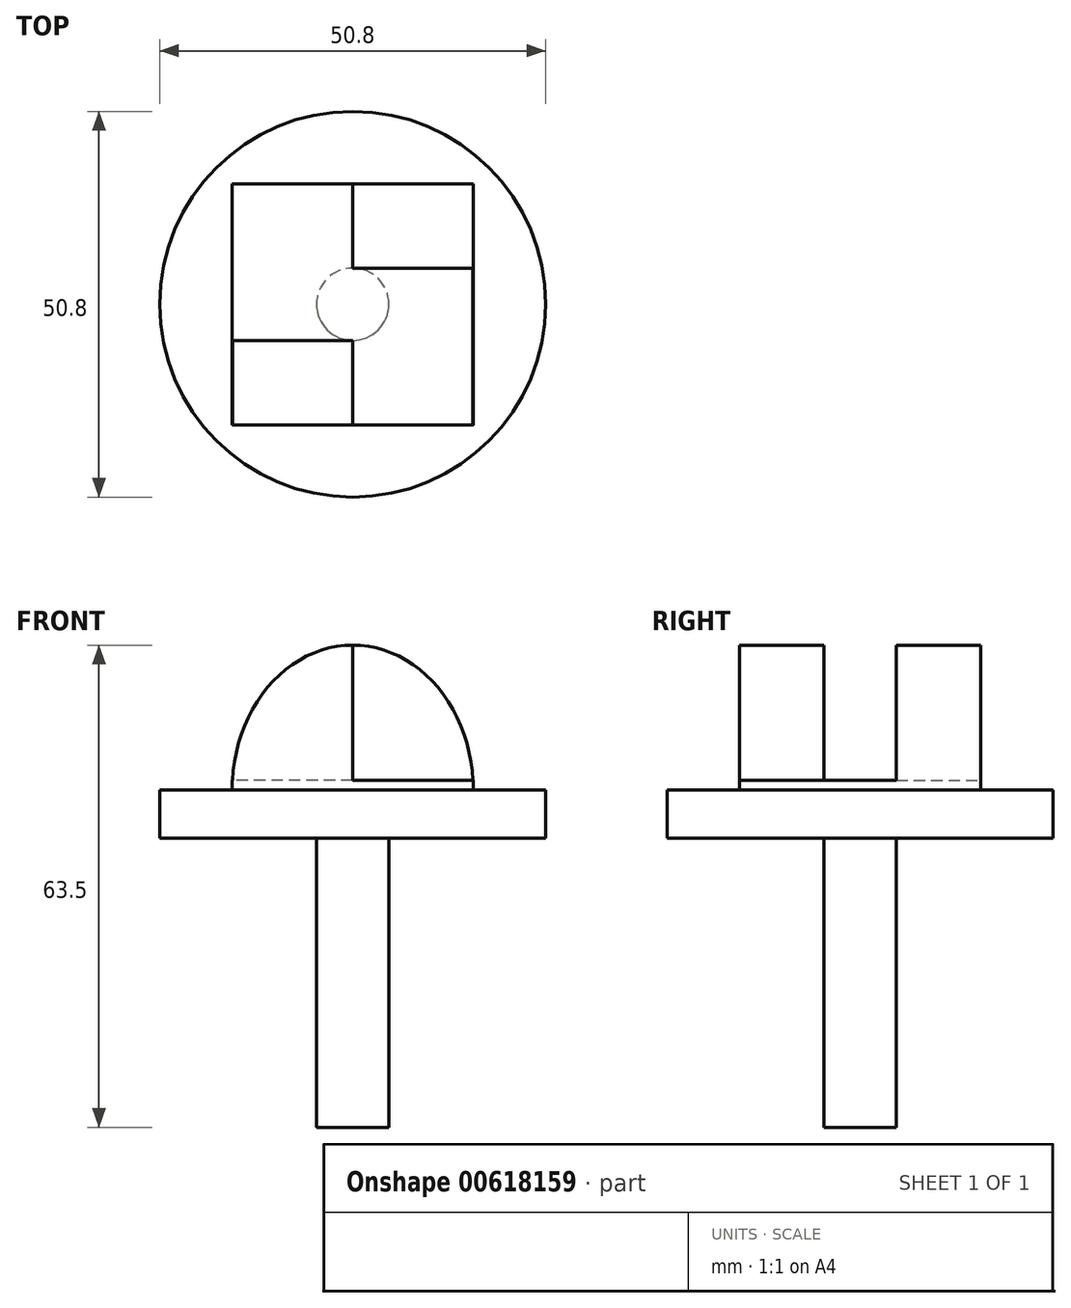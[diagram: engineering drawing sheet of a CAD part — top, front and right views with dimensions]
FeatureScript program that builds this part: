
annotation { "Feature Type Name" : "Feature", "Feature Type Description" : "" }
export const myFeature = defineFeature(function(context is Context, id is Id, definition is map)
    precondition{}
    {
        {
            var Q0;
            Q0=qCreatedBy(makeId("Front.planeOp"),FACE);
            var sketch = newSketch(context, id + "F0", { "sketchPlane" : qUnion([Q0])});
            skLineSegment(sketch, "E0", {"start": v(0, 0) * mm, "end": v(0, 0) * mm});
            skLineSegment(sketch, "E1", {"start": v(0, 0) * mm, "end": v(-4.76, 0) * mm});
            skLineSegment(sketch, "E2", {"start": v(-4.76, -6.35) * mm, "end": v(-4.76, 0) * mm});
            skLineSegment(sketch, "E3", {"start": v(-4.76, -6.35) * mm, "end": v(-25.4, -6.35) * mm});
            skLineSegment(sketch, "E4", {"start": v(-25.4, -6.35) * mm, "end": v(-25.4, 0) * mm});
            skLineSegment(sketch, "E5", {"start": v(-25.4, 0) * mm, "end": v(0, 0) * mm});
            skLineSegment(sketch, "E6", {"start": v(0, 0) * mm, "end": v(0, -6.35) * mm});
            skSolve(sketch);
        }
        {
            var Q0;
            {var subQ0=sQuery(id+"F0.wireOp",EDGE,"E2");Q0=makeQuery(id+"F0.imprint","IMPRINT",FACE,{"disambiguationData":[TD([[makeQuery(id+"F0.imprint","IMPRINT",EDGE,{"derivedFrom":subQ0}),1.0]])]});}
            var Q1;
            Q1=sQuery(id+"F0.wireOp",EDGE,"E6");
            revolve(context, id + "F1", {"entities" : qUnion([Q0]), "axis" : qUnion([Q1]), "revolveType" : RevolveType.FULL});
        }
        {
            var Q0;
            Q0=makeQuery(id+"F1.opRevolve","SWEPT_FACE",FACE,{"disambiguationData":[OSD([sQuery(id+"F0.wireOp",EDGE,"E5")])]});
            var sketch = newSketch(context, id + "F2", { "sketchPlane" : qUnion([Q0])});
            skLineSegment(sketch, "E7.bottom", {"start": v(15.88, -15.87) * mm, "end": v(-15.87, -15.88) * mm});
            skLineSegment(sketch, "E7.top", {"start": v(15.87, 15.88) * mm, "end": v(-15.88, 15.88) * mm});
            skLineSegment(sketch, "E7.left", {"start": v(15.88, -15.87) * mm, "end": v(15.87, 15.88) * mm});
            skLineSegment(sketch, "E7.right", {"start": v(-15.88, -15.88) * mm, "end": v(-15.88, 15.88) * mm});
            skPoint(sketch, "E7.middle", {"position": v(0, 0) * mm});
            skCircle(sketch, "E8.0", {"center": v(0, 0) * mm, "radius": 4.76 * mm});
            skSolve(sketch);
        }
        {
            var Q0;
            Q0=qSketchRegion(id+"F2",true);
            extrude(context, id + "F3", {"entities" : qUnion([Q0]), "operationType" : NewBodyOperationType.ADD, "depth" : 19.05 * mm});
        }
        {
            var Q0;
            Q0=makeQuery(id+"F3.opExtrude","SWEPT_FACE",FACE,{"disambiguationData":[OSD([sQuery(id+"F2.wireOp",EDGE,"E7.left")])]});
            var sketch = newSketch(context, id + "F4", { "sketchPlane" : qUnion([Q0])});
            skLineSegment(sketch, "E9", {"start": v(0, 19.05) * mm, "end": v(0, 0) * mm});
            skCircle(sketch, "E10", {"center": v(0, 6.35) * mm, "radius": 4.76 * mm});
            skLineSegment(sketch, "E11", {"start": v(-4.76, 6.35) * mm, "end": v(-4.76, 19.05) * mm});
            skLineSegment(sketch, "E12", {"start": v(4.76, 6.35) * mm, "end": v(4.76, 19.05) * mm});
            skSolve(sketch);
        }
        {
            var Q0;
            {var subQ5=sQuery(id+"F4.wireOp",EDGE,"E11");Q0=makeQuery(id+"F4.imprint","IMPRINT",FACE,{"disambiguationData":[TD([[makeQuery(id+"F4.imprint","IMPRINT",EDGE,{"derivedFrom":subQ5}),-1.0]])]});}
            var Q1;
            {var subQ0=sQuery(id+"F4.wireOp",EDGE,"E10");var subQ1=sQuery(id+"F4.wireOp",EDGE,"E9");var subQ2=makeQuery(id+"F4.imprint","INTERSECT",VERTEX,{"disambiguationData":[OD(0.0)],"derivedFrom":[subQ1,subQ0]});Q1=makeQuery(id+"F4.imprint","IMPRINT",FACE,{"disambiguationData":[TD([[makeQuery(id+"F4.imprint","IMPRINT",EDGE,{"disambiguationData":[TD([[subQ2,-1.0]])],"derivedFrom":subQ1}),1.0]])]});}
            var Q2;
            {var subQ0=sQuery(id+"F4.wireOp",EDGE,"E10");var subQ1=sQuery(id+"F4.wireOp",EDGE,"E9");var subQ2=makeQuery(id+"F4.imprint","INTERSECT",VERTEX,{"disambiguationData":[OD(0.0)],"derivedFrom":[subQ1,subQ0]});Q2=makeQuery(id+"F4.imprint","IMPRINT",FACE,{"disambiguationData":[TD([[makeQuery(id+"F4.imprint","IMPRINT",EDGE,{"disambiguationData":[TD([[subQ2,-1.0]])],"derivedFrom":subQ1}),-1.0]])]});}
            var Q3;
            {var subQ5=sQuery(id+"F4.wireOp",EDGE,"E12");Q3=makeQuery(id+"F4.imprint","IMPRINT",FACE,{"disambiguationData":[TD([[makeQuery(id+"F4.imprint","IMPRINT",EDGE,{"derivedFrom":subQ5}),1.0]])]});}
            extrude(context, id + "F5", {"entities" : qUnion([Q0, Q1, Q2, Q3]), "operationType" : NewBodyOperationType.REMOVE, "endBound" : BoundingType.THROUGH_ALL, "oppositeDirection" : true, "depth" : 25.4 * mm});
        }
        {
            var Q0;
            Q0=makeQuery(id+"F3.opExtrude","SWEPT_FACE",FACE,{"disambiguationData":[OSD([sQuery(id+"F2.wireOp",EDGE,"E7.bottom")])]});
            var sketch = newSketch(context, id + "F6", { "sketchPlane" : qUnion([Q0])});
            skLineSegment(sketch, "E13.0.0", {"start": v(-15.88, 0) * mm, "end": v(15.88, 0) * mm});
            skLineSegment(sketch, "E13.0.1", {"start": v(15.88, 0) * mm, "end": v(15.88, 19.05) * mm});
            skLineSegment(sketch, "E13.0.2", {"start": v(15.88, 19.05) * mm, "end": v(-15.88, 19.05) * mm});
            skLineSegment(sketch, "E13.0.3", {"start": v(-15.88, 19.05) * mm, "end": v(-15.88, 0) * mm});
            skLineSegment(sketch, "E14", {"start": v(0, 19.05) * mm, "end": v(0, 0) * mm});
            skCircle(sketch, "E15", {"center": v(0, 9.53) * mm, "radius": 6.35 * mm});
            skSolve(sketch);
        }
        {
            var Q0;
            {var subQ0=sQuery(id+"F6.wireOp",EDGE,"E15");var subQ1=sQuery(id+"F6.wireOp",EDGE,"E14");var subQ2=makeQuery(id+"F6.imprint","INTERSECT",VERTEX,{"disambiguationData":[OD(0.0)],"derivedFrom":[subQ1,subQ0]});Q0=makeQuery(id+"F6.imprint","IMPRINT",FACE,{"disambiguationData":[TD([[makeQuery(id+"F6.imprint","IMPRINT",EDGE,{"disambiguationData":[TD([[subQ2,-1.0]])],"derivedFrom":subQ1}),1.0]])]});}
            var Q1;
            {var subQ0=sQuery(id+"F6.wireOp",EDGE,"E15");var subQ1=sQuery(id+"F6.wireOp",EDGE,"E14");var subQ2=makeQuery(id+"F6.imprint","INTERSECT",VERTEX,{"disambiguationData":[OD(0.0)],"derivedFrom":[subQ1,subQ0]});Q1=makeQuery(id+"F6.imprint","IMPRINT",FACE,{"disambiguationData":[TD([[makeQuery(id+"F6.imprint","IMPRINT",EDGE,{"disambiguationData":[TD([[subQ2,-1.0]])],"derivedFrom":subQ1}),-1.0]])]});}
            extrude(context, id + "F7", {"entities" : qUnion([Q0, Q1]), "operationType" : NewBodyOperationType.REMOVE, "endBound" : BoundingType.THROUGH_ALL, "oppositeDirection" : true, "depth" : 25.4 * mm});
        }
        {
            var Q0;
            {var subQ0=sQuery(id+"F2.wireOp",EDGE,"E7.bottom");var subQ1=sQuery(id+"F2.wireOp",EDGE,"E7.right");var subQ2=sQuery(id+"F2.wireOp",EDGE,"E7.left");Q0=makeQuery(id+"F5.boolean.opBoolean","SPLIT",FACE,{"disambiguationData":[TD([makeQuery(id+"F3.opExtrude","SWEPT_FACE",FACE,{"disambiguationData":[OSD([subQ0])]})])],"derivedFrom":makeQuery(id+"F3.opExtrude","CAP_FACE",FACE,{"disambiguationData":[OSD([subQ0,sQuery(id+"F2.wireOp",EDGE,"E7.top"),subQ2,subQ1,sQuery(id+"F2.wireOp",EDGE,"E8.0")])],"isStart":false})});}
            var sketch = newSketch(context, id + "F8", { "sketchPlane" : qUnion([Q0])});
            skLineSegment(sketch, "E16.0", {"start": v(15.88, -15.87) * mm, "end": v(-15.87, -15.88) * mm});
            skLineSegment(sketch, "E17.0", {"start": v(15.88, -15.87) * mm, "end": v(15.87, 15.88) * mm});
            skLineSegment(sketch, "E18.0", {"start": v(15.87, 15.88) * mm, "end": v(-15.88, 15.88) * mm});
            skLineSegment(sketch, "E19.0", {"start": v(-15.88, -15.88) * mm, "end": v(-15.88, 15.88) * mm});
            skLineSegment(sketch, "E20", {"start": v(-15.88, 0) * mm, "end": v(15.88, 0) * mm});
            skLineSegment(sketch, "E21", {"start": v(0, -15.88) * mm, "end": v(0, 15.88) * mm});
            skSolve(sketch);
        }
        {
            var Q0;
            {var subQ0=sQuery(id+"F8.wireOp",EDGE,"E17.0");var subQ1=sQuery(id+"F8.wireOp",EDGE,"E16.0");var subQ2=makeQuery(id+"F8.imprint","INTERSECT",VERTEX,{"derivedFrom":[subQ1,subQ0]});Q0=makeQuery(id+"F8.imprint","IMPRINT",FACE,{"disambiguationData":[TD([[makeQuery(id+"F8.imprint","IMPRINT",EDGE,{"disambiguationData":[TD([[subQ2,-1.0]])],"derivedFrom":subQ1}),-1.0]])]});}
            var Q1;
            {var subQ0=sQuery(id+"F8.wireOp",EDGE,"E17.0");var subQ3=sQuery(id+"F8.wireOp",EDGE,"E20");var subQ4=makeQuery(id+"F8.imprint","INTERSECT",VERTEX,{"derivedFrom":[subQ0,subQ3]});Q1=makeQuery(id+"F8.imprint","IMPRINT",FACE,{"disambiguationData":[TD([[makeQuery(id+"F8.imprint","IMPRINT",EDGE,{"disambiguationData":[TD([[subQ4,1.0]])],"derivedFrom":subQ3}),-1.0]])]});}
            var Q2;
            {var subQ0=sQuery(id+"F8.wireOp",EDGE,"E19.0");var subQ1=sQuery(id+"F8.wireOp",EDGE,"E18.0");var subQ2=makeQuery(id+"F8.imprint","INTERSECT",VERTEX,{"derivedFrom":[subQ1,subQ0]});Q2=makeQuery(id+"F8.imprint","IMPRINT",FACE,{"disambiguationData":[TD([[makeQuery(id+"F8.imprint","IMPRINT",EDGE,{"disambiguationData":[TD([[subQ2,1.0]])],"derivedFrom":subQ1}),1.0]])]});}
            extrude(context, id + "F9", {"entities" : qUnion([Q0, Q1, Q2]), "operationType" : NewBodyOperationType.REMOVE, "oppositeDirection" : true, "depth" : 17.78 * mm});
        }
        {
            var Q0;
            Q0=makeQuery(id+"F3.opExtrude","SWEPT_FACE",FACE,{"disambiguationData":[OSD([sQuery(id+"F2.wireOp",EDGE,"E7.top")])]});
            var sketch = newSketch(context, id + "F10", { "sketchPlane" : qUnion([Q0])});
            skLineSegment(sketch, "E22.0", {"start": v(-15.87, 19.05) * mm, "end": v(-15.87, 0) * mm});
            skLineSegment(sketch, "E23.0", {"start": v(15.87, 19.05) * mm, "end": v(15.87, 0) * mm});
            skLineSegment(sketch, "E24", {"start": v(-15.87, 0) * mm, "end": v(15.87, 0) * mm});
            skEllipse(sketch, "E25", {"center": v(0, 0) * mm, "majorRadius": 19.05 * mm, "minorRadius": 15.87 * mm, "majorAxis": v(0, 1)});
            skLineSegment(sketch, "E26.0", {"start": v(-15.87, 19.05) * mm, "end": v(0, 19.05) * mm});
            skLineSegment(sketch, "E27.0", {"start": v(15.88, 19.05) * mm, "end": v(0, 19.05) * mm});
            skSolve(sketch);
        }
        {
            var Q0;
            {var subQ0=sQuery(id+"F10.wireOp",EDGE,"E22.0");Q0=makeQuery(id+"F10.imprint","IMPRINT",FACE,{"disambiguationData":[TD([[makeQuery(id+"F10.imprint","IMPRINT",EDGE,{"derivedFrom":subQ0}),1.0]])]});}
            var Q1;
            {var subQ4=sQuery(id+"F10.wireOp",EDGE,"E27.0");Q1=makeQuery(id+"F10.imprint","IMPRINT",FACE,{"disambiguationData":[TD([[makeQuery(id+"F10.imprint","IMPRINT",EDGE,{"derivedFrom":subQ4}),1.0]])]});}
            extrude(context, id + "F11", {"entities" : qUnion([Q0, Q1]), "operationType" : NewBodyOperationType.REMOVE, "endBound" : BoundingType.THROUGH_ALL, "oppositeDirection" : true, "depth" : 25.4 * mm});
        }
        {
            var Q0;
            Q0=makeQuery(id+"F3.opExtrude","SWEPT_FACE",FACE,{"disambiguationData":[OSD([sQuery(id+"F2.wireOp",EDGE,"E7.top")])]});
            var sketch = newSketch(context, id + "F12", { "sketchPlane" : qUnion([Q0])});
            skCircle(sketch, "E28", {"center": v(0, 9.53) * mm, "radius": 4.76 * mm});
            skSolve(sketch);
        }
        {
            var Q0;
            Q0=qSketchRegion(id+"F12",true);
            var Q1;
            Q1=makeQuery(id+"F3.opExtrude","SWEPT_FACE",FACE,{"disambiguationData":[OSD([sQuery(id+"F2.wireOp",EDGE,"E7.bottom")])]});
            extrude(context, id + "F13", {"entities" : qUnion([Q0]), "endBound" : BoundingType.UP_TO_SURFACE, "oppositeDirection" : true, "endBoundEntityFace" : qUnion([Q1]), "depth" : 25.4 * mm});
        }
        {
            var Q0;
            Q0=makeQuery(id+"F3.opExtrude","SWEPT_FACE",FACE,{"disambiguationData":[OSD([sQuery(id+"F2.wireOp",EDGE,"E7.top")])]});
            var sketch = newSketch(context, id + "F14", { "sketchPlane" : qUnion([Q0])});
            skCircle(sketch, "E29.0.0", {"center": v(0, 9.53) * mm, "radius": 4.76 * mm});
            skArc(sketch, "E30.0", {"start": v(0, 3.17) * mm, "mid": v(-6.35, 9.53) * mm, "end": v(0, 15.88) * mm});
            skArc(sketch, "E31.0", {"start": v(0, 15.88) * mm, "mid": v(6.35, 9.53) * mm, "end": v(0, 3.17) * mm});
            skCircle(sketch, "E32", {"center": v(-14.29, 9.52) * mm, "radius": 9.53 * mm});
            skLineSegment(sketch, "E33", {"start": v(-14.29, 9.52) * mm, "end": v(-4.76, 9.52) * mm});
            skCircle(sketch, "E34", {"center": v(14.29, 9.53) * mm, "radius": 9.53 * mm});
            skLineSegment(sketch, "E35", {"start": v(0, 15.88) * mm, "end": v(0, 3.17) * mm});
            skSolve(sketch);
        }
        {
            var Q0;
            {var subQ1=sQuery(id+"F14.wireOp",EDGE,"E29.0.0");var subQ3=sQuery(id+"F14.wireOp",EDGE,"E35");var subQ4=makeQuery(id+"F14.imprint","INTERSECT",VERTEX,{"disambiguationData":[OD(0.0)],"derivedFrom":[subQ1,subQ3]});Q0=makeQuery(id+"F14.imprint","IMPRINT",FACE,{"disambiguationData":[TD([[makeQuery(id+"F14.imprint","IMPRINT",EDGE,{"disambiguationData":[TD([[subQ4,-1.0]])],"derivedFrom":subQ1}),-1.0]])]});}
            var Q1;
            {var subQ0=sQuery(id+"F14.wireOp",EDGE,"E33");var subQ1=sQuery(id+"F14.wireOp",EDGE,"E30.0");var subQ2=makeQuery(id+"F14.imprint","INTERSECT",VERTEX,{"derivedFrom":[subQ1,subQ0]});Q1=makeQuery(id+"F14.imprint","IMPRINT",FACE,{"disambiguationData":[TD([[makeQuery(id+"F14.imprint","IMPRINT",EDGE,{"disambiguationData":[TD([[subQ2,-1.0]])],"derivedFrom":subQ1}),-1.0]])]});}
            var Q2;
            {var subQ0=sQuery(id+"F14.wireOp",EDGE,"E32");var subQ1=sQuery(id+"F14.wireOp",EDGE,"E30.0");var subQ2=makeQuery(id+"F14.imprint","INTERSECT",VERTEX,{"disambiguationData":[OD(0.0)],"derivedFrom":[subQ1,subQ0]});Q2=makeQuery(id+"F14.imprint","IMPRINT",FACE,{"disambiguationData":[TD([[makeQuery(id+"F14.imprint","IMPRINT",EDGE,{"disambiguationData":[TD([[subQ2,-1.0]])],"derivedFrom":subQ1}),-1.0]])]});}
            var Q3;
            {var subQ1=sQuery(id+"F14.wireOp",EDGE,"E29.0.0");var subQ3=sQuery(id+"F14.wireOp",EDGE,"E35");var subQ4=makeQuery(id+"F14.imprint","INTERSECT",VERTEX,{"disambiguationData":[OD(1.0)],"derivedFrom":[subQ1,subQ3]});Q3=makeQuery(id+"F14.imprint","IMPRINT",FACE,{"disambiguationData":[TD([[makeQuery(id+"F14.imprint","IMPRINT",EDGE,{"disambiguationData":[TD([[subQ4,1.0]])],"derivedFrom":subQ1}),-1.0]])]});}
            var Q4;
            Q4=makeQuery(id+"F5.boolean.opBoolean","COPY",FACE,{"derivedFrom":makeQuery(id+"F5.opExtrude","SWEPT_FACE",FACE,{"disambiguationData":[OSD([sQuery(id+"F4.wireOp",EDGE,"E12")])]})});
            extrude(context, id + "F15", {"entities" : qUnion([Q0, Q1, Q2, Q3]), "operationType" : NewBodyOperationType.ADD, "endBound" : BoundingType.UP_TO_SURFACE, "oppositeDirection" : true, "endBoundEntityFace" : qUnion([Q4]), "depth" : 25.4 * mm});
        }
        {
            var Q0;
            Q0=makeQuery(id+"F3.opExtrude","SWEPT_FACE",FACE,{"disambiguationData":[OSD([sQuery(id+"F2.wireOp",EDGE,"E7.bottom")])]});
            var sketch = newSketch(context, id + "F16", { "sketchPlane" : qUnion([Q0])});
            skCircle(sketch, "E36.0.0", {"center": v(0, 9.53) * mm, "radius": 4.76 * mm});
            skArc(sketch, "E37.0", {"start": v(0, 15.88) * mm, "mid": v(-6.35, 9.53) * mm, "end": v(0, 3.17) * mm});
            skLineSegment(sketch, "E38", {"start": v(0, 15.88) * mm, "end": v(0, 3.17) * mm});
            skSolve(sketch);
        }
        {
            var Q0;
            {var subQ4=sQuery(id+"F16.wireOp",EDGE,"E37.0");Q0=makeQuery(id+"F16.imprint","IMPRINT",FACE,{"disambiguationData":[TD([[makeQuery(id+"F16.imprint","IMPRINT",EDGE,{"derivedFrom":subQ4}),1.0]])]});}
            var Q1;
            Q1=makeQuery(id+"F5.boolean.opBoolean","COPY",FACE,{"derivedFrom":makeQuery(id+"F5.opExtrude","SWEPT_FACE",FACE,{"disambiguationData":[OSD([sQuery(id+"F4.wireOp",EDGE,"E11")])]})});
            extrude(context, id + "F17", {"entities" : qUnion([Q0]), "operationType" : NewBodyOperationType.ADD, "endBound" : BoundingType.UP_TO_SURFACE, "oppositeDirection" : true, "endBoundEntityFace" : qUnion([Q1]), "depth" : 25.4 * mm});
        }
        {
            var Q0;
            {var subQ11=sQuery(id+"F14.wireOp",EDGE,"E32");var subQ12=sQuery(id+"F14.wireOp",EDGE,"E30.0");var subQ13=makeQuery(id+"F14.imprint","INTERSECT",VERTEX,{"disambiguationData":[OD(0.0)],"derivedFrom":[subQ12,subQ11]});Q0=makeQuery(id+"F14.imprint","IMPRINT",FACE,{"disambiguationData":[TD([[makeQuery(id+"F14.imprint","IMPRINT",EDGE,{"disambiguationData":[TD([[subQ13,1.0]])],"derivedFrom":subQ11}),-1.0]])]});}
            var Q1;
            {var subQ0=sQuery(id+"F14.wireOp",EDGE,"E31.0");var subQ11=sQuery(id+"F14.wireOp",EDGE,"E34");var subQ12=makeQuery(id+"F14.imprint","INTERSECT",VERTEX,{"disambiguationData":[OD(1.0)],"derivedFrom":[subQ0,subQ11]});Q1=makeQuery(id+"F14.imprint","IMPRINT",FACE,{"disambiguationData":[TD([[makeQuery(id+"F14.imprint","IMPRINT",EDGE,{"disambiguationData":[TD([[subQ12,-1.0]])],"derivedFrom":subQ11}),-1.0]])]});}
            var Q2;
            {var subQ1=sQuery(id+"F14.wireOp",EDGE,"E29.0.0");var subQ16=sQuery(id+"F14.wireOp",EDGE,"E34");var subQ18=makeQuery(id+"F14.imprint","INTERSECT",VERTEX,{"derivedFrom":[subQ1,subQ16]});Q2=makeQuery(id+"F14.imprint","IMPRINT",FACE,{"disambiguationData":[TD([[makeQuery(id+"F14.imprint","IMPRINT",EDGE,{"disambiguationData":[TD([[subQ18,-1.0]])],"derivedFrom":subQ16}),-1.0]])]});}
            var Q3;
            {var subQ1=sQuery(id+"F14.wireOp",EDGE,"E29.0.0");var subQ3=sQuery(id+"F14.wireOp",EDGE,"E35");var subQ4=makeQuery(id+"F14.imprint","INTERSECT",VERTEX,{"disambiguationData":[OD(1.0)],"derivedFrom":[subQ1,subQ3]});Q3=makeQuery(id+"F14.imprint","IMPRINT",FACE,{"disambiguationData":[TD([[makeQuery(id+"F14.imprint","IMPRINT",EDGE,{"disambiguationData":[TD([[subQ4,1.0]])],"derivedFrom":subQ1}),-1.0]])]});}
            var Q4;
            Q4=makeQuery(id+"F3.opExtrude","SWEPT_FACE",FACE,{"disambiguationData":[OSD([sQuery(id+"F2.wireOp",EDGE,"E7.bottom")])]});
            extrude(context, id + "F18", {"entities" : qUnion([Q0, Q1, Q2, Q3]), "endBound" : BoundingType.UP_TO_SURFACE, "oppositeDirection" : true, "endBoundEntityFace" : qUnion([Q4]), "depth" : 25.4 * mm});
        }
        {
            var Q0;
            Q0=makeQuery(id+"F1.opRevolve","SWEPT_BODY",BODY,{"disambiguationData":[OSD([sQuery(id+"F0.wireOp",EDGE,"E2"),sQuery(id+"F0.wireOp",EDGE,"E3"),sQuery(id+"F0.wireOp",EDGE,"E4"),sQuery(id+"F0.wireOp",EDGE,"E5")])]});
            var Q1;
            Q1=makeQuery(id+"F18.opExtrude","SWEPT_BODY",BODY,{"disambiguationData":[OSD([sQuery(id+"F2.wireOp",EDGE,"E7.top"),sQuery(id+"F14.wireOp",EDGE,"E29.0.0"),sQuery(id+"F14.wireOp",EDGE,"E32"),sQuery(id+"F14.wireOp",EDGE,"E34")])]});
            booleanBodies(context, id + "F19", {"operationType" : BooleanOperationType.UNION, "tools" : qUnion([Q0, Q1])});
        }
        {
            var Q0;
            Q0=makeQuery(id+"F9.boolean.opBoolean","COPY",FACE,{"derivedFrom":makeQuery(id+"F9.opExtrude","CAP_FACE",FACE,{"disambiguationData":[OSD([sQuery(id+"F8.wireOp",EDGE,"E16.0"),sQuery(id+"F8.wireOp",EDGE,"E17.0"),sQuery(id+"F8.wireOp",EDGE,"E20"),sQuery(id+"F8.wireOp",EDGE,"E21")])],"isStart":false})});
            var sketch = newSketch(context, id + "F20", { "sketchPlane" : qUnion([Q0])});
            skLineSegment(sketch, "E39.0", {"start": v(-15.88, -15.88) * mm, "end": v(-15.88, 15.88) * mm});
            skLineSegment(sketch, "E40.0", {"start": v(15.88, -15.87) * mm, "end": v(15.87, 15.88) * mm});
            skLineSegment(sketch, "E41", {"start": v(-15.87, -15.87) * mm, "end": v(15.88, 15.88) * mm, "construction": true});
            skLineSegment(sketch, "E42.bottom", {"start": v(15.88, 4.76) * mm, "end": v(-15.87, 4.76) * mm});
            skLineSegment(sketch, "E42.top", {"start": v(15.88, -4.76) * mm, "end": v(-15.87, -4.76) * mm});
            skLineSegment(sketch, "E42.left", {"start": v(15.88, 4.76) * mm, "end": v(15.88, -4.76) * mm});
            skLineSegment(sketch, "E42.right", {"start": v(-15.87, 4.76) * mm, "end": v(-15.87, -4.76) * mm});
            skPoint(sketch, "E42.middle", {"position": v(0, 0) * mm});
            skSolve(sketch);
        }
        {
            var Q0;
            Q0=makeQuery(id+"F20.imprint","IMPRINT",FACE,{"disambiguationData":[TD([[makeQuery(id+"F20.imprint","IMPRINT",EDGE,{"derivedFrom":sQuery(id+"F20.wireOp",EDGE,"E42.bottom")}),1.0]])]});
            var Q1;
            {var subQ14=sQuery(id+"F8.wireOp",EDGE,"E20");var subQ16=sQuery(id+"F8.wireOp",EDGE,"E17.0");var subQ22=makeQuery(id+"F9.boolean.opBoolean","COPY",EDGE,{"derivedFrom":makeQuery(id+"F9.opExtrude","CAP_EDGE",EDGE,{"disambiguationData":[OSD([subQ14]),TDD([makeQuery(id+"F8.imprint","IMPRINT",EDGE,{"disambiguationData":[TD([[makeQuery(id+"F8.imprint","INTERSECT",VERTEX,{"derivedFrom":[subQ16,subQ14]}),1.0]])],"derivedFrom":subQ14})])],"isStart":false})});Q1=makeQuery(id+"F20.imprint","IMPRINT",FACE,{"disambiguationData":[TD([[makeQuery(id+"F20.imprint","IMPRINT",EDGE,{"derivedFrom":subQ22}),-1.0]])]});}
            extrude(context, id + "F21", {"entities" : qUnion([Q0, Q1]), "operationType" : NewBodyOperationType.REMOVE, "depth" : 25.4 * mm});
        }
        {
            var Q0;
            {var subQ0=sQuery(id+"F8.wireOp",EDGE,"E21");var subQ1=sQuery(id+"F8.wireOp",EDGE,"E20");var subQ2=sQuery(id+"F8.wireOp",EDGE,"E18.0");Q0=makeQuery(id+"F21.boolean.opBoolean","MERGE",FACE,{"derivedFrom":[makeQuery(id+"F11.boolean.opBoolean","MERGE",FACE,{"derivedFrom":[makeQuery(id+"F9.boolean.opBoolean","COPY",FACE,{"derivedFrom":makeQuery(id+"F9.opExtrude","CAP_FACE",FACE,{"disambiguationData":[OSD([subQ2,sQuery(id+"F8.wireOp",EDGE,"E19.0"),subQ1,subQ0])],"isStart":false})}),makeQuery(id+"F11.opExtrude","SWEPT_FACE",FACE,{"disambiguationData":[OSD([subQ2])]})]}),makeQuery(id+"F9.boolean.opBoolean","COPY",FACE,{"derivedFrom":makeQuery(id+"F9.opExtrude","CAP_FACE",FACE,{"disambiguationData":[OSD([sQuery(id+"F8.wireOp",EDGE,"E16.0"),sQuery(id+"F8.wireOp",EDGE,"E17.0"),subQ1,subQ0])],"isStart":false})}),makeQuery(id+"F21.opExtrude","CAP_FACE",FACE,{"disambiguationData":[OSD([sQuery(id+"F20.wireOp",EDGE,"E42.bottom"),sQuery(id+"F20.wireOp",EDGE,"E42.top"),sQuery(id+"F20.wireOp",EDGE,"E42.left"),sQuery(id+"F20.wireOp",EDGE,"E42.right")])],"isStart":true})]});}
            var sketch = newSketch(context, id + "F22", { "sketchPlane" : qUnion([Q0])});
            skLineSegment(sketch, "E43.bottom", {"start": v(15.84, -15.88) * mm, "end": v(-15.84, -15.88) * mm});
            skLineSegment(sketch, "E43.top", {"start": v(0, 15.88) * mm, "end": v(-15.84, 15.88) * mm});
            skLineSegment(sketch, "E43.left", {"start": v(15.84, -15.88) * mm, "end": v(15.84, 15.88) * mm});
            skLineSegment(sketch, "E43.right", {"start": v(-15.84, 4.76) * mm, "end": v(-15.84, 15.88) * mm});
            skPoint(sketch, "E43.middle", {"position": v(0, 0) * mm});
            skLineSegment(sketch, "E44.0", {"start": v(0, 4.76) * mm, "end": v(0, 15.88) * mm});
            skLineSegment(sketch, "E45.0", {"start": v(0, -15.88) * mm, "end": v(0, -4.76) * mm});
            skLineSegment(sketch, "E46", {"start": v(0, -4.76) * mm, "end": v(15.84, -4.76) * mm});
            skLineSegment(sketch, "E47", {"start": v(0, 4.76) * mm, "end": v(-15.84, 4.76) * mm});
            skSolve(sketch);
        }
        {
            var Q0;
            Q0=qSketchRegion(id+"F22",true);
            extrude(context, id + "F23", {"entities" : qUnion([Q0]), "operationType" : NewBodyOperationType.REMOVE, "depth" : 25.4 * mm});
        }
        {
            var Q0;
            Q0=makeQuery(id+"F18.opExtrude","SWEPT_FACE",FACE,{"disambiguationData":[OSD([sQuery(id+"F2.wireOp",EDGE,"E7.top")])]});
            var sketch = newSketch(context, id + "F24", { "sketchPlane" : qUnion([Q0])});
            skCircle(sketch, "E48.0.0", {"center": v(0, 0) * mm, "radius": 4.76 * mm});
            skSolve(sketch);
        }
        {
            var Q0;
            Q0=qSketchRegion(id+"F24",true);
            extrude(context, id + "F25", {"entities" : qUnion([Q0]), "operationType" : NewBodyOperationType.ADD, "depth" : 44.45 * mm});
        }
    });
